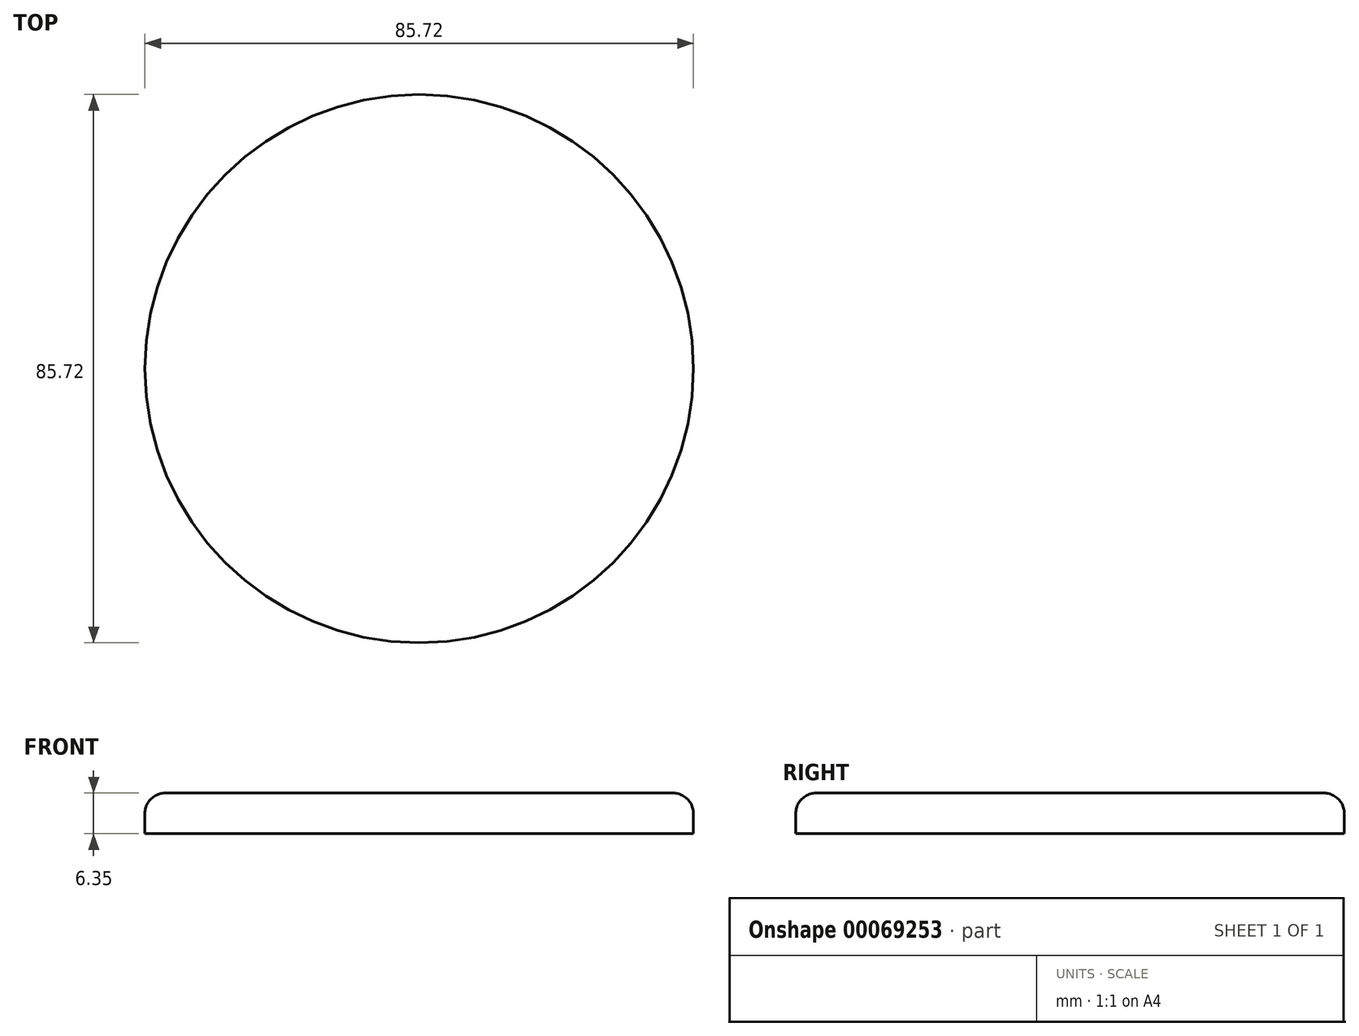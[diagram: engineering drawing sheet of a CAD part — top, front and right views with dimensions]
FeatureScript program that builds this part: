
annotation { "Feature Type Name" : "Feature", "Feature Type Description" : "" }
export const myFeature = defineFeature(function(context is Context, id is Id, definition is map)
    precondition{}
    {
        {
            var Q0;
            Q0=qCreatedBy(makeId("Top.planeOp"),FACE);
            var sketch = newSketch(context, id + "F0", { "sketchPlane" : qUnion([Q0])});
            skCircle(sketch, "E0", {"center": v(0, 0) * mm, "radius": 42.86 * mm});
            skSolve(sketch);
        }
        {
            var Q0;
            Q0 = qSketchRegion(id + "F0", true);
            extrude(context, id + "F1", {"entities" : qUnion([Q0]), "oppositeDirection" : true, "depth" : 6.35 * mm});
        }
        {
            var Q0;
            Q0=makeQuery(id+"F1.opExtrude","CAP_EDGE",EDGE,{"disambiguationData":[OSD([sQuery(id+"F0.wireOp",EDGE,"E0")])],"isStart":true});
            fillet(context, id + "F2", {"entities" : qUnion([Q0]), "radius" : 3.17 * mm, "tangentPropagation" : true, "allowEdgeOverflow" : false});
        }
    });
